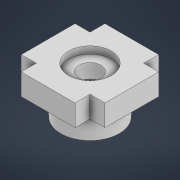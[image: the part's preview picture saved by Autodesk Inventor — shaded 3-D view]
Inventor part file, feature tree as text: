
AUTODESK INVENTOR PART (.ipt)
format: ipt  version: 2021 (Build 250183000, 183)  size: 309,760 bytes
history: native  units: mm
features: extrude x5, sketch x4, other x1, plane x1
ambient origin geometry x8: Origin, YZ Plane, XZ Plane, XY Plane, X Axis, Y Axis, Z Axis, Center Point
bodies: Volumenkörper1 (feature_tree)
feature tree (11):
  other  "Zahnrad_innen"
  extrude  "Extrusion1"  Depth=11.75mm
  sketch  "Skizze2"  dims[d3=11.75mm d12=3.0mm d13=0.0mm]
  plane  "Arbeitsebene1"
  extrude  "Extrusion4"  Depth=3.0mm TaperAngle=0.0deg
  extrude  "Extrusion5"  Depth=6.0mm
  extrude  "Extrusion6"  Depth=3.5mm TaperAngle=0.0deg
  extrude  "Extrusion7"  Depth=2.1mm
  sketch  "Skizze1"  dims[d1=7.0mm d2=11.75mm]
  sketch  "Skizze5"  dims[d14=6.0mm d20=6.0mm]
  sketch  "Skizze6"  dims[d21=8.2mm d22=3.5mm d23=0.0mm d24=2.1mm d25=2.1mm d26=2.1mm d27=2.1mm d28=2.1mm d29=2.1mm d30=2.1mm d31=2.1mm d32=6.0mm d33=0.0mm d34=1.0mm d35=0.0mm d38=3.1mm d39=10.0mm d40=0.0mm d15=0.5mm d16=0.872665mm d17=0.5mm d18=0.872665mm d36=0.5mm d37=0.872665mm]
